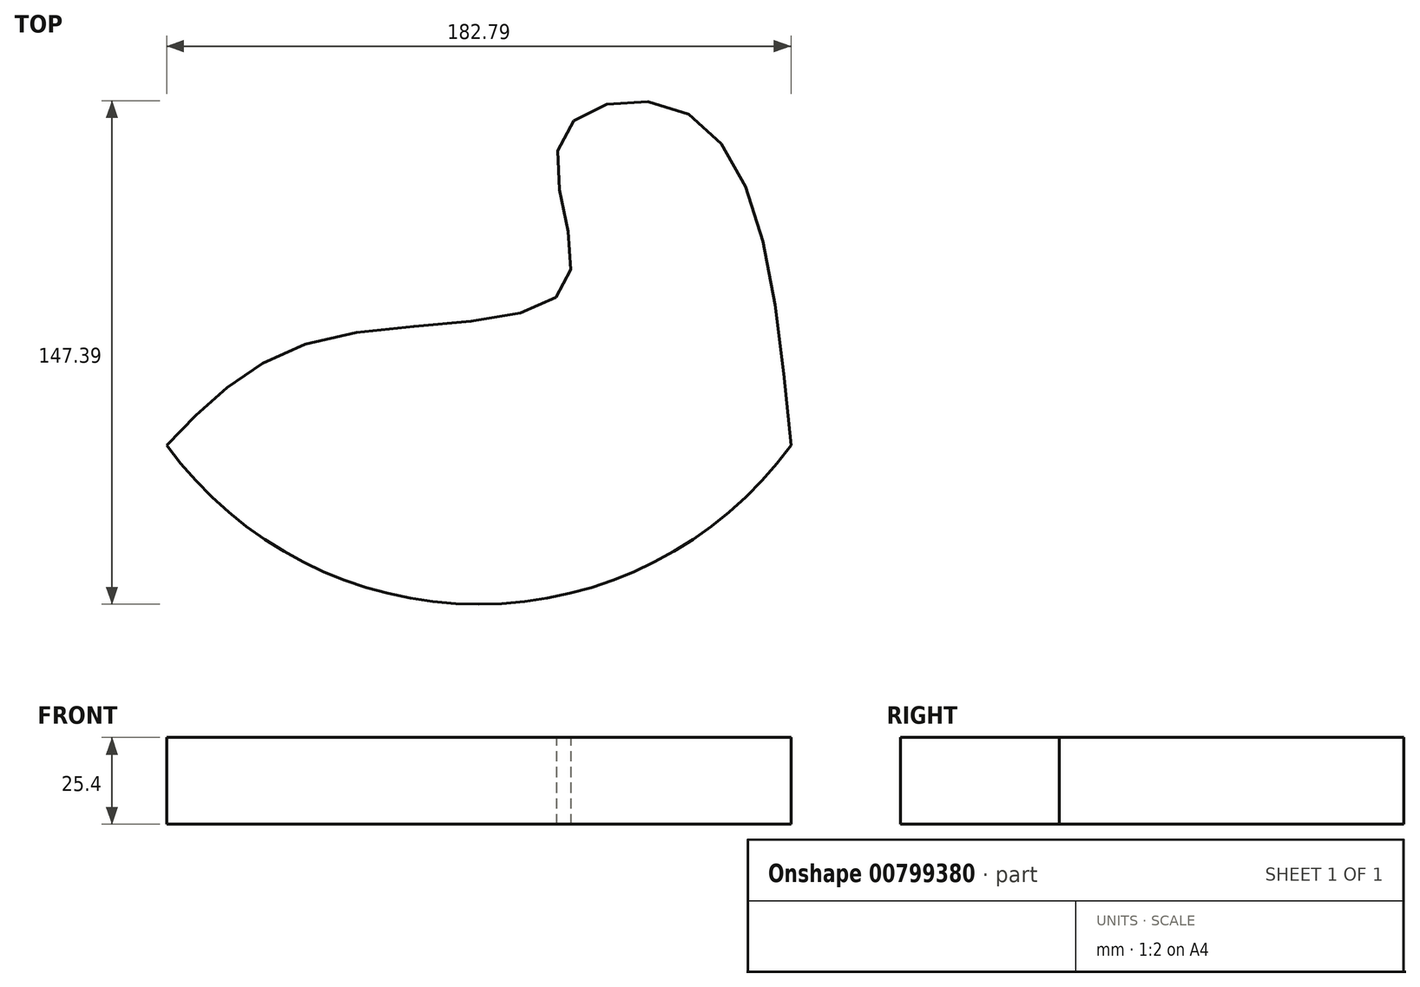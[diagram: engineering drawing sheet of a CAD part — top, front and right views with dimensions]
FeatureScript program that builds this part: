
annotation { "Feature Type Name" : "Feature", "Feature Type Description" : "" }
export const myFeature = defineFeature(function(context is Context, id is Id, definition is map)
    precondition{}
    {
        {
            var Q0;
            Q0=qCreatedBy(makeId("Top.planeOp"),FACE);
            var sketch = newSketch(context, id + "F0", { "sketchPlane" : qUnion([Q0])});
            skFitSpline(sketch, "E0", {"points": [v(-133.97, 0) * mm, v(-86.71, 31.43) * mm, v(-17.16, 46.59) * mm, v(-18.5, 89.83) * mm, v(19.4, 96.52) * mm, v(48.82, 0) * mm], "startDerivative": vector(193.2, 202.4) * mm, "endDerivative": vector(46.04, -485.5) * mm});
            skArc(sketch, "E1", {"start": v(-133.97, 0) * mm, "mid": v(-42.58, -46.56) * mm, "end": v(48.82, 0) * mm});
            skSolve(sketch);
        }
        {
            var Q0;
            Q0=makeQuery(id+"F0.imprint","IMPRINT",FACE,{"disambiguationData":[TD([[makeQuery(id+"F0.imprint","IMPRINT",EDGE,{"derivedFrom":sQuery(id+"F0.wireOp",EDGE,"E0")}),-1.0]])]});
            extrude(context, id + "F1", {"entities" : qUnion([Q0]), "depth" : 25.4 * mm, "offsetDistance" : 25.4 * mm});
        }
    });
